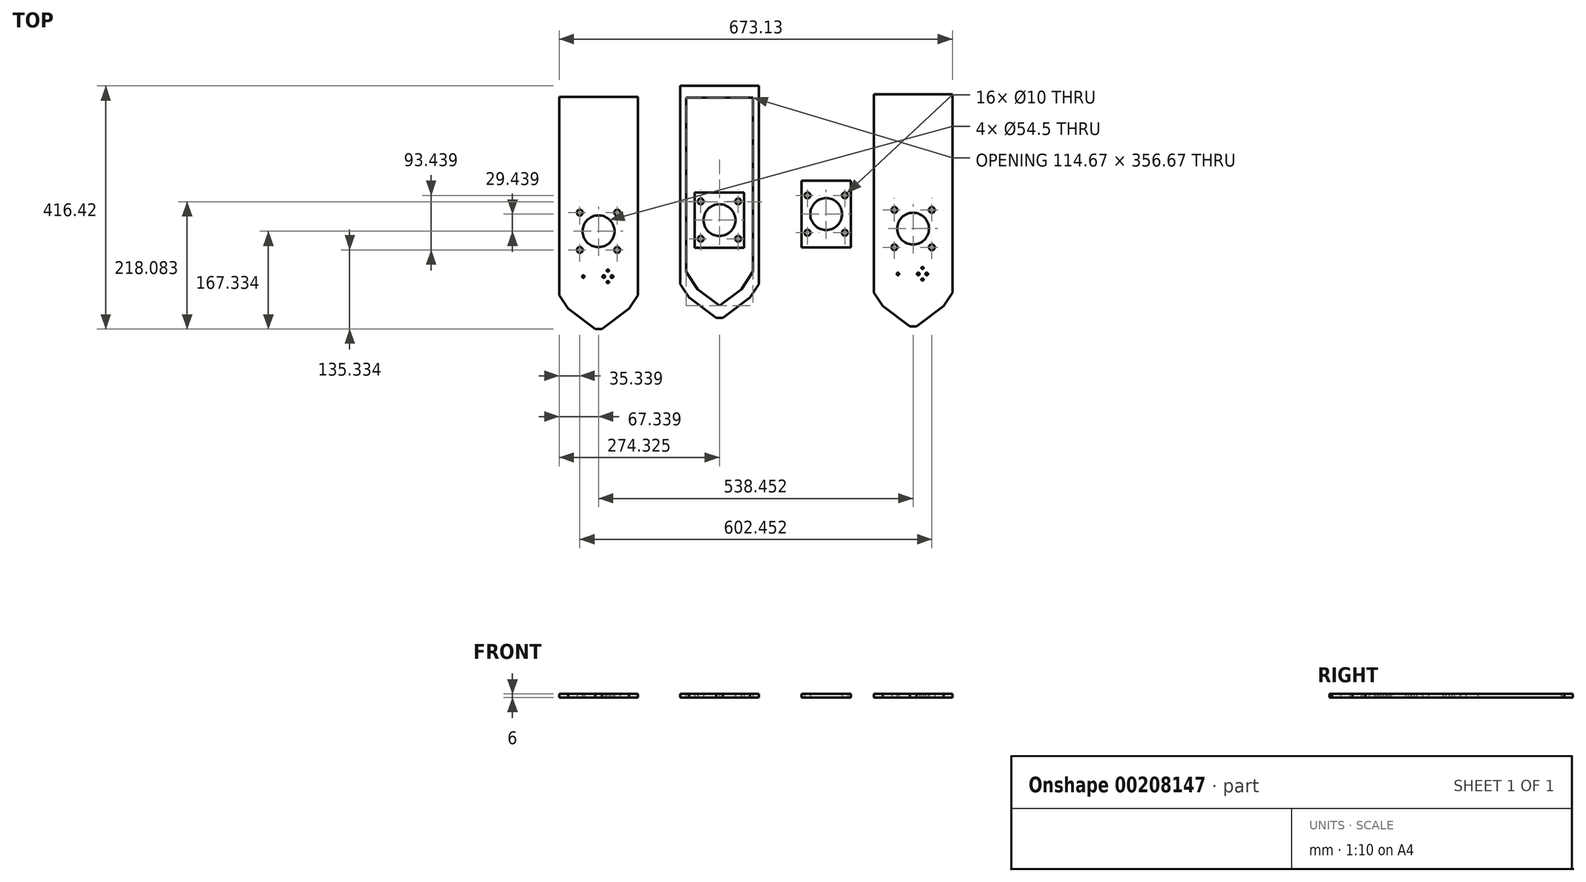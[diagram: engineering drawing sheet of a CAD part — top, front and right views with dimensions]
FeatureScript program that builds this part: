
annotation { "Feature Type Name" : "Feature", "Feature Type Description" : "" }
export const myFeature = defineFeature(function(context is Context, id is Id, definition is map)
    precondition{}
    {
        {
            var Q0;
            Q0=qCreatedBy(makeId("Top.planeOp"),FACE);
            var sketch = newSketch(context, id + "F0", { "sketchPlane" : qUnion([Q0])});
            skLineSegment(sketch, "E0", {"start": v(-312.45, 182.98) * mm, "end": v(-312.45, -156.85) * mm});
            skLineSegment(sketch, "E1", {"start": v(-312.45, -156.85) * mm, "end": v(-297.33, -179.52) * mm});
            skLineSegment(sketch, "E2", {"start": v(-297.33, -179.52) * mm, "end": v(-250.89, -214.35) * mm});
            skLineSegment(sketch, "E3", {"start": v(-250.89, -214.35) * mm, "end": v(-239.33, -214.35) * mm});
            skLineSegment(sketch, "E4", {"start": v(-239.33, -214.35) * mm, "end": v(-192.89, -179.52) * mm});
            skLineSegment(sketch, "E5", {"start": v(-192.89, -179.52) * mm, "end": v(-177.78, -156.85) * mm});
            skLineSegment(sketch, "E6", {"start": v(-177.78, -156.85) * mm, "end": v(-177.78, 182.98) * mm});
            skLineSegment(sketch, "E7", {"start": v(-177.78, 182.98) * mm, "end": v(-312.45, 182.98) * mm});
            skCircle(sketch, "E8", {"center": v(-277.11, -79.02) * mm, "radius": 5 * mm});
            skCircle(sketch, "E9.0.1.0", {"center": v(-277.11, -15.02) * mm, "radius": 5 * mm});
            skCircle(sketch, "E9.1.0.0", {"center": v(-213.11, -79.02) * mm, "radius": 5 * mm});
            skCircle(sketch, "E9.1.1.0", {"center": v(-213.11, -15.02) * mm, "radius": 5 * mm});
            skCircle(sketch, "E10", {"center": v(-245.11, -47.02) * mm, "radius": 27.25 * mm});
            skLineSegment(sketch, "E11.top", {"start": v(-287.45, -104.35) * mm, "end": v(-202.78, -104.35) * mm, "construction": true});
            skLineSegment(sketch, "E12", {"start": v(-245.11, -214.35) * mm, "end": v(-245.11, -104.35) * mm, "construction": true});
            skLineSegment(sketch, "E13", {"start": v(-229.11, -104.35) * mm, "end": v(-229.11, -161.46) * mm, "construction": true});
            skCircle(sketch, "E14", {"center": v(-229.11, -114.35) * mm, "radius": 1.75 * mm});
            skCircle(sketch, "E15", {"center": v(-229.11, -134.1) * mm, "radius": 1.75 * mm});
            skCircle(sketch, "E16", {"center": v(-221.91, -124.6) * mm, "radius": 2.25 * mm});
            skCircle(sketch, "E17", {"center": v(-236.21, -124.6) * mm, "radius": 2.25 * mm});
            skCircle(sketch, "E18", {"center": v(-271.21, -124.6) * mm, "radius": 2 * mm});
            skSolve(sketch);
        }
        {
            var Q0;
            Q0=qCreatedBy(makeId("Top.planeOp"),FACE);
            var sketch = newSketch(context, id + "F1", { "sketchPlane" : qUnion([Q0])});
            skLineSegment(sketch, "E19", {"start": v(-105.46, 202.07) * mm, "end": v(-105.46, -137.77) * mm});
            skLineSegment(sketch, "E20", {"start": v(-105.46, -137.77) * mm, "end": v(-90.35, -160.44) * mm});
            skLineSegment(sketch, "E21", {"start": v(-90.35, -160.44) * mm, "end": v(-43.9, -195.27) * mm});
            skLineSegment(sketch, "E22", {"start": v(-43.9, -195.27) * mm, "end": v(-32.35, -195.27) * mm});
            skLineSegment(sketch, "E23", {"start": v(-32.35, -195.27) * mm, "end": v(14.1, -160.44) * mm});
            skLineSegment(sketch, "E24", {"start": v(14.1, -160.44) * mm, "end": v(29.21, -137.77) * mm});
            skLineSegment(sketch, "E25", {"start": v(29.21, -137.77) * mm, "end": v(29.21, 202.07) * mm});
            skLineSegment(sketch, "E26", {"start": v(29.21, 202.07) * mm, "end": v(-105.46, 202.07) * mm});
            skLineSegment(sketch, "E27", {"start": v(-95.46, 182.07) * mm, "end": v(-95.46, -116.7) * mm});
            skLineSegment(sketch, "E28", {"start": v(-95.46, -116.7) * mm, "end": v(-75.6, -146.5) * mm});
            skLineSegment(sketch, "E29", {"start": v(-75.6, -146.5) * mm, "end": v(-38.12, -174.6) * mm});
            skLineSegment(sketch, "E30", {"start": v(-38.12, -174.6) * mm, "end": v(-0.64, -146.5) * mm});
            skLineSegment(sketch, "E31", {"start": v(-0.64, -146.5) * mm, "end": v(19.21, -116.05) * mm});
            skLineSegment(sketch, "E32", {"start": v(19.21, -116.05) * mm, "end": v(19.21, 182.07) * mm});
            skLineSegment(sketch, "E33", {"start": v(19.21, 182.07) * mm, "end": v(-95.46, 182.07) * mm});
            skCircle(sketch, "E34", {"center": v(-70.12, -59.93) * mm, "radius": 5 * mm});
            skCircle(sketch, "E35.0.1.0", {"center": v(-70.12, 4.07) * mm, "radius": 5 * mm});
            skCircle(sketch, "E35.1.0.0", {"center": v(-6.12, -59.93) * mm, "radius": 5 * mm});
            skCircle(sketch, "E35.1.1.0", {"center": v(-6.12, 4.07) * mm, "radius": 5 * mm});
            skCircle(sketch, "E36", {"center": v(-38.12, -27.93) * mm, "radius": 27.25 * mm});
            skLineSegment(sketch, "E37.bottom", {"start": v(-80.46, 19.57) * mm, "end": v(4.21, 19.57) * mm});
            skLineSegment(sketch, "E37.top", {"start": v(-80.46, -75.43) * mm, "end": v(4.21, -75.43) * mm});
            skLineSegment(sketch, "E37.left", {"start": v(-80.46, 19.57) * mm, "end": v(-80.46, -75.43) * mm});
            skLineSegment(sketch, "E37.right", {"start": v(4.21, 19.57) * mm, "end": v(4.21, -75.43) * mm});
            skSolve(sketch);
        }
        {
            var Q0;
            Q0 = qSketchRegion(id + "F0", true);
            var Q1;
            Q1 = qSketchRegion(id + "F1", true);
            extrude(context, id + "F2", {"entities" : qUnion([Q0, Q1]), "depth" : 6 * mm});
        }
        {
            var Q0;
            Q0=makeQuery(id+"F1.imprint","IMPRINT",FACE,{"disambiguationData":[TD([[makeQuery(id+"F1.imprint","IMPRINT",EDGE,{"derivedFrom":sQuery(id+"F1.wireOp",EDGE,"E34")}),-1.0]])]});
            extrude(context, id + "F3", {"entities" : qUnion([Q0]), "depth" : 6 * mm});
        }
        {
            var Q0;
            Q0=qCreatedBy(makeId("Top.planeOp"),FACE);
            var sketch = newSketch(context, id + "F4", { "sketchPlane" : qUnion([Q0])});
            skCircle(sketch, "E38", {"center": v(112.53, -49.58) * mm, "radius": 5 * mm});
            skCircle(sketch, "E39.0.1.0", {"center": v(112.53, 14.42) * mm, "radius": 5 * mm});
            skCircle(sketch, "E39.1.0.0", {"center": v(176.53, -49.58) * mm, "radius": 5 * mm});
            skCircle(sketch, "E39.1.1.0", {"center": v(176.53, 14.42) * mm, "radius": 5 * mm});
            skCircle(sketch, "E40", {"center": v(144.53, -17.58) * mm, "radius": 27.25 * mm});
            skLineSegment(sketch, "E41.bottom", {"start": v(102.2, 39.76) * mm, "end": v(186.87, 39.76) * mm});
            skLineSegment(sketch, "E41.top", {"start": v(102.2, -74.91) * mm, "end": v(186.87, -74.91) * mm});
            skLineSegment(sketch, "E41.left", {"start": v(102.2, 39.76) * mm, "end": v(102.2, -74.91) * mm});
            skLineSegment(sketch, "E41.right", {"start": v(186.87, 39.76) * mm, "end": v(186.87, -74.91) * mm});
            skSolve(sketch);
        }
        {
            var Q0;
            Q0=makeQuery(id+"F4.imprint","IMPRINT",FACE,{"disambiguationData":[TD([[makeQuery(id+"F4.imprint","IMPRINT",EDGE,{"derivedFrom":sQuery(id+"F4.wireOp",EDGE,"E38")}),-1.0]])]});
            extrude(context, id + "F5", {"entities" : qUnion([Q0]), "depth" : 6 * mm});
        }
        {
            var Q0;
            Q0=qCreatedBy(makeId("Top.planeOp"),FACE);
            var sketch = newSketch(context, id + "F6", { "sketchPlane" : qUnion([Q0])});
            skLineSegment(sketch, "E42", {"start": v(226, 187.48) * mm, "end": v(226, -152.36) * mm});
            skLineSegment(sketch, "E43", {"start": v(226, -152.36) * mm, "end": v(241.12, -175.03) * mm});
            skLineSegment(sketch, "E44", {"start": v(241.12, -175.03) * mm, "end": v(287.56, -209.86) * mm});
            skLineSegment(sketch, "E45", {"start": v(287.56, -209.86) * mm, "end": v(299.12, -209.86) * mm});
            skLineSegment(sketch, "E46", {"start": v(299.12, -209.86) * mm, "end": v(345.56, -175.03) * mm});
            skLineSegment(sketch, "E47", {"start": v(345.56, -175.03) * mm, "end": v(360.68, -152.36) * mm});
            skLineSegment(sketch, "E48", {"start": v(360.68, -152.36) * mm, "end": v(360.68, 187.48) * mm});
            skLineSegment(sketch, "E49", {"start": v(360.68, 187.48) * mm, "end": v(226, 187.48) * mm});
            skCircle(sketch, "E50", {"center": v(261.34, -74.52) * mm, "radius": 5 * mm});
            skCircle(sketch, "E51.0.1.0", {"center": v(261.34, -10.52) * mm, "radius": 5 * mm});
            skCircle(sketch, "E51.1.0.0", {"center": v(325.34, -74.52) * mm, "radius": 5 * mm});
            skCircle(sketch, "E51.1.1.0", {"center": v(325.34, -10.52) * mm, "radius": 5 * mm});
            skCircle(sketch, "E52", {"center": v(293.34, -42.52) * mm, "radius": 27.25 * mm});
            skLineSegment(sketch, "E53.top", {"start": v(251, -99.86) * mm, "end": v(335.68, -99.86) * mm, "construction": true});
            skLineSegment(sketch, "E54", {"start": v(293.34, -209.86) * mm, "end": v(293.34, -99.86) * mm, "construction": true});
            skLineSegment(sketch, "E55", {"start": v(309.34, -99.86) * mm, "end": v(309.34, -156.97) * mm, "construction": true});
            skCircle(sketch, "E56", {"center": v(309.34, -109.86) * mm, "radius": 1.75 * mm});
            skCircle(sketch, "E57", {"center": v(309.34, -129.6) * mm, "radius": 1.75 * mm});
            skCircle(sketch, "E58", {"center": v(316.54, -120.1) * mm, "radius": 2.25 * mm});
            skCircle(sketch, "E59", {"center": v(302.24, -120.1) * mm, "radius": 2.25 * mm});
            skCircle(sketch, "E60", {"center": v(267.24, -120.1) * mm, "radius": 2 * mm});
            skSolve(sketch);
        }
        {
            var Q0;
            Q0=makeQuery(id+"F6.imprint","IMPRINT",FACE,{"disambiguationData":[TD([[makeQuery(id+"F6.imprint","IMPRINT",EDGE,{"derivedFrom":sQuery(id+"F6.wireOp",EDGE,"E42")}),1.0]])]});
            extrude(context, id + "F7", {"entities" : qUnion([Q0]), "depth" : 6 * mm});
        }
    });
